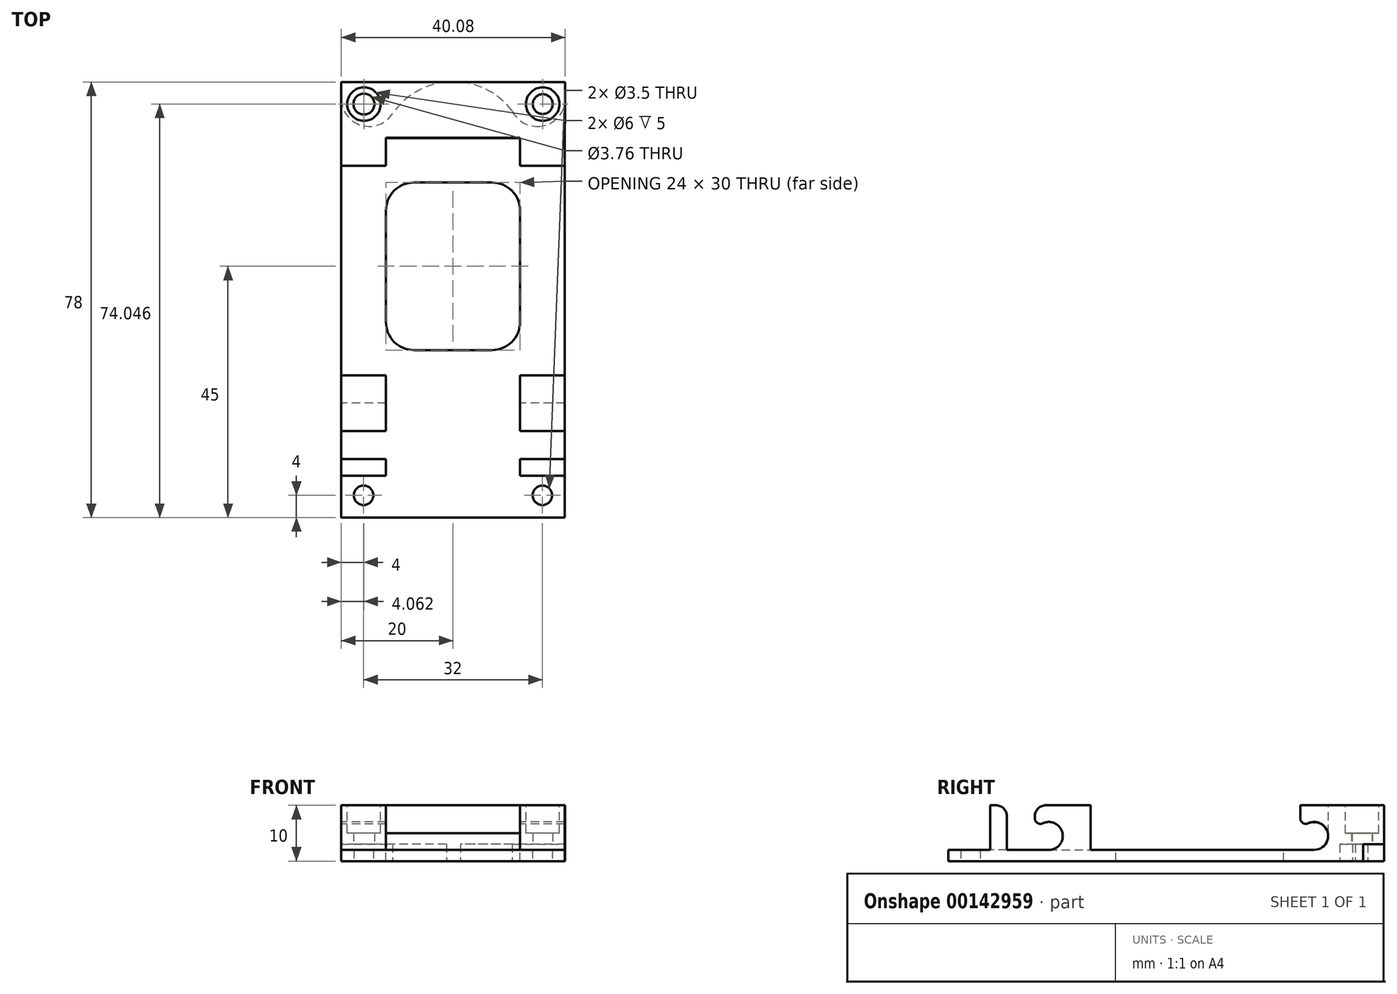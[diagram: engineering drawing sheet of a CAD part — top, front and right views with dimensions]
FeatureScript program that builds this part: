
annotation { "Feature Type Name" : "Feature", "Feature Type Description" : "" }
export const myFeature = defineFeature(function(context is Context, id is Id, definition is map)
    precondition{}
    {
        {
            var Q0;
            Q0=qCreatedBy(makeId("Top.planeOp"),FACE);
            var sketch = newSketch(context, id + "F0", { "sketchPlane" : qUnion([Q0])});
            skLineSegment(sketch, "E0.bottom", {"start": v(20, -39) * mm, "end": v(-20, -39) * mm});
            skLineSegment(sketch, "E0.top", {"start": v(20, 39) * mm, "end": v(-20, 39) * mm});
            skLineSegment(sketch, "E0.left", {"start": v(20, -39) * mm, "end": v(20, 39) * mm});
            skLineSegment(sketch, "E0.right", {"start": v(-20, -39) * mm, "end": v(-20, 39) * mm});
            skPoint(sketch, "E0.middle", {"position": v(0, 0) * mm});
            skCircle(sketch, "E1", {"center": v(-16, 35) * mm, "radius": 1.75 * mm});
            skCircle(sketch, "E2", {"center": v(16, 35) * mm, "radius": 1.75 * mm});
            skCircle(sketch, "E3", {"center": v(-16, -35) * mm, "radius": 1.75 * mm});
            skCircle(sketch, "E4", {"center": v(16, -35) * mm, "radius": 1.75 * mm});
            skSolve(sketch);
        }
        {
            var Q0;
            Q0=makeQuery(id+"F0.imprint","IMPRINT",FACE,{"disambiguationData":[TD([[makeQuery(id+"F0.imprint","IMPRINT",EDGE,{"derivedFrom":sQuery(id+"F0.wireOp",EDGE,"E0.bottom")}),-1.0]])]});
            extrude(context, id + "F1", {"entities" : qUnion([Q0]), "depth" : 2 * mm});
        }
        {
            var Q0;
            Q0=qCreatedBy(makeId("Top.planeOp"),FACE);
            var sketch = newSketch(context, id + "F2", { "sketchPlane" : qUnion([Q0])});
            skLineSegment(sketch, "E5.0", {"start": v(20, 24) * mm, "end": v(-20, 24) * mm});
            skLineSegment(sketch, "E6.0", {"start": v(20, -31.5) * mm, "end": v(12, -31.5) * mm});
            skLineSegment(sketch, "E7.0", {"start": v(20, -28.5) * mm, "end": v(12, -28.5) * mm});
            skLineSegment(sketch, "E8.0", {"start": v(20, -23.5) * mm, "end": v(12, -23.5) * mm});
            skLineSegment(sketch, "E9.trimOffspring", {"start": v(-12, -23.5) * mm, "end": v(-20, -23.5) * mm});
            skLineSegment(sketch, "E10.trimOffspring", {"start": v(-12, -28.5) * mm, "end": v(-20, -28.5) * mm});
            skLineSegment(sketch, "E11.trimOffspring", {"start": v(-12, -31.5) * mm, "end": v(-20, -31.5) * mm});
            skLineSegment(sketch, "E12.0", {"start": v(-12, -13.5) * mm, "end": v(-20, -13.5) * mm});
            skLineSegment(sketch, "E13.0", {"start": v(20, -13.5) * mm, "end": v(12, -13.5) * mm});
            skLineSegment(sketch, "E14", {"start": v(-12, -31.5) * mm, "end": v(-12, -28.5) * mm});
            skLineSegment(sketch, "E15", {"start": v(-20, -31.5) * mm, "end": v(-20, -28.5) * mm});
            skLineSegment(sketch, "E16", {"start": v(-20, -23.5) * mm, "end": v(-20, -13.5) * mm});
            skLineSegment(sketch, "E17", {"start": v(-12, -23.5) * mm, "end": v(-12, -13.5) * mm});
            skLineSegment(sketch, "E18", {"start": v(12, -13.5) * mm, "end": v(12, -23.5) * mm});
            skLineSegment(sketch, "E19", {"start": v(20, -13.5) * mm, "end": v(20, -23.5) * mm});
            skLineSegment(sketch, "E20", {"start": v(12, -31.5) * mm, "end": v(12, -28.5) * mm});
            skLineSegment(sketch, "E21", {"start": v(20, -31.5) * mm, "end": v(20, -28.5) * mm});
            skLineSegment(sketch, "E22", {"start": v(-12, 24) * mm, "end": v(-20, 24) * mm});
            skLineSegment(sketch, "E23", {"start": v(-20, 24) * mm, "end": v(-20, 39) * mm});
            skLineSegment(sketch, "E24", {"start": v(20.08, 39) * mm, "end": v(20, 24) * mm});
            skLineSegment(sketch, "E25.0", {"start": v(20, 39) * mm, "end": v(-20, 39) * mm});
            skLineSegment(sketch, "E26", {"start": v(-20, 39) * mm, "end": v(20.08, 39) * mm});
            skLineSegment(sketch, "E27", {"start": v(-20, 24) * mm, "end": v(20, 24) * mm});
            skSolve(sketch);
        }
        {
            var Q0;
            Q0 = qSketchRegion(id + "F2", true);
            extrude(context, id + "F3", {"entities" : qUnion([Q0]), "operationType" : NewBodyOperationType.ADD, "depth" : 10 * mm});
        }
        {
            var Q0;
            Q0=qCreatedBy(makeId("Right.planeOp"),FACE);
            var sketch = newSketch(context, id + "F4", { "sketchPlane" : qUnion([Q0])});
            skLineSegment(sketch, "E28.0", {"start": v(29, 4.5) * mm, "end": v(29, 4.5) * mm});
            skLineSegment(sketch, "E29", {"start": v(26.5, 2) * mm, "end": v(24, 2) * mm});
            skLineSegment(sketch, "E30.0", {"start": v(-18.5, 4.5) * mm, "end": v(-18.5, 4.5) * mm});
            skLineSegment(sketch, "E31", {"start": v(-21, 2) * mm, "end": v(-23.5, 2) * mm});
            skPoint(sketch, "E32.visualSharp", {"position": v(-18.5, 7) * mm});
            skPoint(sketch, "E33.visualSharp", {"position": v(-18.5, 2) * mm});
            skArc(sketch, "E33.filletArc", {"start": v(-21, 2) * mm, "mid": v(-19.23, 2.73) * mm, "end": v(-18.5, 4.5) * mm});
            skLineSegment(sketch, "E34", {"start": v(-23.5, 7.66) * mm, "end": v(-23.5, 2) * mm});
            skPoint(sketch, "E35.visualSharp", {"position": v(29, 7) * mm});
            skPoint(sketch, "E36.visualSharp", {"position": v(29, 2) * mm});
            skLineSegment(sketch, "E37.0", {"start": v(-28.5, 7.5) * mm, "end": v(-28.5, 2) * mm});
            skLineSegment(sketch, "E38.0", {"start": v(-31.5, 10) * mm, "end": v(-31, 10) * mm});
            skLineSegment(sketch, "E39.0", {"start": v(-21, 10) * mm, "end": v(-13.5, 10) * mm});
            skPoint(sketch, "E40.visualSharp", {"position": v(-28.5, 10) * mm});
            skPoint(sketch, "E41.visualSharp", {"position": v(-23.5, 10) * mm});
            skLineSegment(sketch, "E42", {"start": v(-31, 10) * mm, "end": v(-31, 10) * mm});
            skLineSegment(sketch, "E43", {"start": v(-21, 10) * mm, "end": v(-21, 10) * mm});
            skLineSegment(sketch, "E44", {"start": v(-28.5, 7.5) * mm, "end": v(-28.5, 7.5) * mm});
            skArc(sketch, "E45", {"start": v(-21, 2) * mm, "mid": v(-18.56, 5.05) * mm, "end": v(-22.07, 6.76) * mm});
            skLineSegment(sketch, "E46", {"start": v(-23.5, 7.66) * mm, "end": v(-23.5, 10) * mm});
            skArc(sketch, "E47.filletArc", {"start": v(-23.5, 7.66) * mm, "mid": v(-23.03, 6.82) * mm, "end": v(-22.07, 6.76) * mm});
            skArc(sketch, "E48", {"start": v(26.5, 2) * mm, "mid": v(28.94, 5.05) * mm, "end": v(25.43, 6.76) * mm});
            skArc(sketch, "E49.filletArc", {"start": v(24, 7.66) * mm, "mid": v(24.47, 6.82) * mm, "end": v(25.43, 6.76) * mm});
            skLineSegment(sketch, "E50.2", {"start": v(-28.5, 2) * mm, "end": v(-23.5, 2) * mm});
            skLineSegment(sketch, "E51", {"start": v(24, 7.66) * mm, "end": v(24, 2) * mm});
            skSolve(sketch);
        }
        {
            var Q0;
            Q0 = qSketchRegion(id + "F4", true);
            extrude(context, id + "F5", {"entities" : qUnion([Q0]), "operationType" : NewBodyOperationType.REMOVE, "depth" : 45 * mm, "symmetric" : true});
        }
        {
            var Q0;
            Q0=qCreatedBy(makeId("Right.planeOp"),FACE);
            var sketch = newSketch(context, id + "F6", { "sketchPlane" : qUnion([Q0])});
            skLineSegment(sketch, "E52.0", {"start": v(-31.5, 10) * mm, "end": v(-30.5, 10) * mm});
            skLineSegment(sketch, "E53.0", {"start": v(-28.5, 8) * mm, "end": v(-28.5, 2) * mm});
            skPoint(sketch, "E54.visualSharp", {"position": v(-28.5, 10) * mm});
            skArc(sketch, "E54.filletArc", {"start": v(-28.5, 8) * mm, "mid": v(-29.09, 9.41) * mm, "end": v(-30.5, 10) * mm});
            skLineSegment(sketch, "E55.0", {"start": v(-13.5, 10) * mm, "end": v(-21.5, 10) * mm});
            skPoint(sketch, "E56.visualSharp", {"position": v(-23.5, 10) * mm});
            skArc(sketch, "E56.filletArc", {"start": v(-21.5, 10) * mm, "mid": v(-22.91, 9.41) * mm, "end": v(-23.5, 8) * mm});
            skLineSegment(sketch, "E57", {"start": v(-30.5, 10) * mm, "end": v(-28.5, 10) * mm});
            skLineSegment(sketch, "E58", {"start": v(-23.5, 8) * mm, "end": v(-23.5, 10) * mm});
            skLineSegment(sketch, "E59", {"start": v(-28.5, 10) * mm, "end": v(-28.5, 8) * mm});
            skLineSegment(sketch, "E60", {"start": v(-21.5, 10) * mm, "end": v(-23.5, 10) * mm});
            skSolve(sketch);
        }
        {
            var Q0;
            Q0 = qSketchRegion(id + "F6", true);
            extrude(context, id + "F7", {"entities" : qUnion([Q0]), "operationType" : NewBodyOperationType.REMOVE, "depth" : 45 * mm, "symmetric" : true});
        }
        {
            var Q0;
            Q0=qCreatedBy(makeId("Top.planeOp"),FACE);
            var sketch = newSketch(context, id + "F8", { "sketchPlane" : qUnion([Q0])});
            skCircle(sketch, "E61", {"center": v(16.06, 35.05) * mm, "radius": 1.77 * mm});
            skCircle(sketch, "E62", {"center": v(-15.94, 35.05) * mm, "radius": 1.88 * mm});
            skSolve(sketch);
        }
        {
            var Q0;
            Q0 = qSketchRegion(id + "F8", true);
            extrude(context, id + "F9", {"entities" : qUnion([Q0]), "operationType" : NewBodyOperationType.REMOVE, "depth" : 12 * mm});
        }
        {
            var Q0;
            Q0=qCreatedBy(makeId("Top.planeOp"),FACE);
            var sketch = newSketch(context, id + "F10", { "sketchPlane" : qUnion([Q0])});
            skCircle(sketch, "E63.0", {"center": v(-15.94, 35.05) * mm, "radius": 1.88 * mm});
            skCircle(sketch, "E64.0", {"center": v(16.06, 35.05) * mm, "radius": 1.77 * mm});
            skLineSegment(sketch, "E65.0", {"start": v(-15, 31.05) * mm, "end": v(-15, 31.05) * mm});
            skLineSegment(sketch, "E66.0", {"start": v(-20, 39) * mm, "end": v(20.12, 39.05) * mm});
            skLineSegment(sketch, "E67", {"start": v(-20, 39) * mm, "end": v(-20, 36.05) * mm});
            skLineSegment(sketch, "E68", {"start": v(20.12, 39.05) * mm, "end": v(20.13, 36.06) * mm});
            skPoint(sketch, "E69.visualSharp", {"position": v(20.14, 31.05) * mm});
            skArc(sketch, "E69.filletArc", {"start": v(15.13, 31.05) * mm, "mid": v(18.67, 32.52) * mm, "end": v(20.13, 36.06) * mm});
            skPoint(sketch, "E70.visualSharp", {"position": v(-20, 31.05) * mm});
            skArc(sketch, "E70.filletArc", {"start": v(-20, 36.05) * mm, "mid": v(-18.54, 32.51) * mm, "end": v(-15, 31.05) * mm});
            skLineSegment(sketch, "E71.trimOffspring", {"start": v(15.07, 31.05) * mm, "end": v(15.13, 31.05) * mm});
            skPoint(sketch, "E72.visualSharp", {"position": v(10.07, 31.05) * mm});
            skArc(sketch, "E72.filletArc", {"start": v(10.58, 33.84) * mm, "mid": v(12.42, 31.8) * mm, "end": v(15.07, 31.05) * mm});
            skPoint(sketch, "E73.visualSharp", {"position": v(-10, 31.05) * mm});
            skArc(sketch, "E73.filletArc", {"start": v(-15, 31.05) * mm, "mid": v(-12.61, 31.65) * mm, "end": v(-10.8, 33.33) * mm});
            skArc(sketch, "E74", {"start": v(10.58, 33.84) * mm, "mid": v(-0.24, 39.06) * mm, "end": v(-10.8, 33.33) * mm});
            skSolve(sketch);
        }
        {
            var Q0;
            Q0 = qSketchRegion(id + "F10", true);
            extrude(context, id + "F11", {"entities" : qUnion([Q0]), "operationType" : NewBodyOperationType.REMOVE, "depth" : 3 * mm});
        }
        {
            var Q0;
            Q0=makeQuery(id+"F3.opExtrude","CAP_FACE",FACE,{"disambiguationData":[OSD([sQuery(id+"F2.wireOp",EDGE,"E24"),sQuery(id+"F2.wireOp",EDGE,"E23"),sQuery(id+"F2.wireOp",EDGE,"E26"),sQuery(id+"F2.wireOp",EDGE,"E27")])],"isStart":false});
            var sketch = newSketch(context, id + "F12", { "sketchPlane" : qUnion([Q0])});
            skCircle(sketch, "E75", {"center": v(-15.94, 35.05) * mm, "radius": 3 * mm});
            skCircle(sketch, "E76", {"center": v(16.06, 35.05) * mm, "radius": 3 * mm});
            skSolve(sketch);
        }
        {
            var Q0;
            Q0 = qSketchRegion(id + "F12", true);
            extrude(context, id + "F13", {"entities" : qUnion([Q0]), "operationType" : NewBodyOperationType.REMOVE, "oppositeDirection" : true, "depth" : 5 * mm});
        }
        {
            var Q0;
            Q0=makeQuery(id+"F5.boolean.opBoolean","MERGE",FACE,{"derivedFrom":[makeQuery(id+"F1.opExtrude","CAP_FACE",FACE,{"disambiguationData":[OSD([sQuery(id+"F0.wireOp",EDGE,"E0.bottom"),sQuery(id+"F0.wireOp",EDGE,"E0.top"),sQuery(id+"F0.wireOp",EDGE,"E0.left"),sQuery(id+"F0.wireOp",EDGE,"E0.right"),sQuery(id+"F0.wireOp",EDGE,"E1"),sQuery(id+"F0.wireOp",EDGE,"E2"),sQuery(id+"F0.wireOp",EDGE,"E3"),sQuery(id+"F0.wireOp",EDGE,"E4")])],"isStart":false}),makeQuery(id+"F5.opExtrude","SWEPT_FACE",FACE,{"disambiguationData":[OSD([sQuery(id+"F4.wireOp",EDGE,"E29")])]}),makeQuery(id+"F5.opExtrude","SWEPT_FACE",FACE,{"disambiguationData":[OSD([sQuery(id+"F4.wireOp",EDGE,"E31")])]})]});
            var sketch = newSketch(context, id + "F14", { "sketchPlane" : qUnion([Q0])});
            skLineSegment(sketch, "E77.bottom", {"start": v(-7, -9) * mm, "end": v(7, -9) * mm});
            skLineSegment(sketch, "E77.top", {"start": v(-7, 21) * mm, "end": v(7, 21) * mm});
            skLineSegment(sketch, "E77.left", {"start": v(-12, -4) * mm, "end": v(-12, 16) * mm});
            skLineSegment(sketch, "E77.right", {"start": v(12, -4) * mm, "end": v(12, 16) * mm});
            skPoint(sketch, "E78.visualSharp", {"position": v(12, 21) * mm});
            skArc(sketch, "E78.filletArc", {"start": v(12, 16) * mm, "mid": v(10.54, 19.54) * mm, "end": v(7, 21) * mm});
            skPoint(sketch, "E79.visualSharp", {"position": v(12, -9) * mm});
            skArc(sketch, "E79.filletArc", {"start": v(7, -9) * mm, "mid": v(10.54, -7.54) * mm, "end": v(12, -4) * mm});
            skPoint(sketch, "E80.visualSharp", {"position": v(-12, -9) * mm});
            skArc(sketch, "E80.filletArc", {"start": v(-12, -4) * mm, "mid": v(-10.54, -7.54) * mm, "end": v(-7, -9) * mm});
            skArc(sketch, "E81.filletArc", {"start": v(-7, 21) * mm, "mid": v(-10.54, 19.54) * mm, "end": v(-12, 16) * mm});
            skSolve(sketch);
        }
        {
            var Q0;
            Q0 = qSketchRegion(id + "F14", true);
            extrude(context, id + "F15", {"entities" : qUnion([Q0]), "operationType" : NewBodyOperationType.REMOVE, "oppositeDirection" : true, "depth" : 3 * mm});
        }
        {
            var Q0;
            Q0=makeQuery(id+"F3.opExtrude","CAP_FACE",FACE,{"disambiguationData":[OSD([sQuery(id+"F2.wireOp",EDGE,"E24"),sQuery(id+"F2.wireOp",EDGE,"E23"),sQuery(id+"F2.wireOp",EDGE,"E26"),sQuery(id+"F2.wireOp",EDGE,"E27")])],"isStart":false});
            var sketch = newSketch(context, id + "F16", { "sketchPlane" : qUnion([Q0])});
            skLineSegment(sketch, "E82.bottom", {"start": v(-12, 24) * mm, "end": v(12, 24) * mm});
            skLineSegment(sketch, "E82.top", {"start": v(-12, 29) * mm, "end": v(12, 29) * mm});
            skLineSegment(sketch, "E82.left", {"start": v(-12, 24) * mm, "end": v(-12, 29) * mm});
            skLineSegment(sketch, "E82.right", {"start": v(12, 24) * mm, "end": v(12, 29) * mm});
            skSolve(sketch);
        }
        {
            var Q0;
            Q0 = qSketchRegion(id + "F16", true);
            extrude(context, id + "F17", {"entities" : qUnion([Q0]), "operationType" : NewBodyOperationType.REMOVE, "oppositeDirection" : true, "depth" : 5 * mm});
        }
    });
